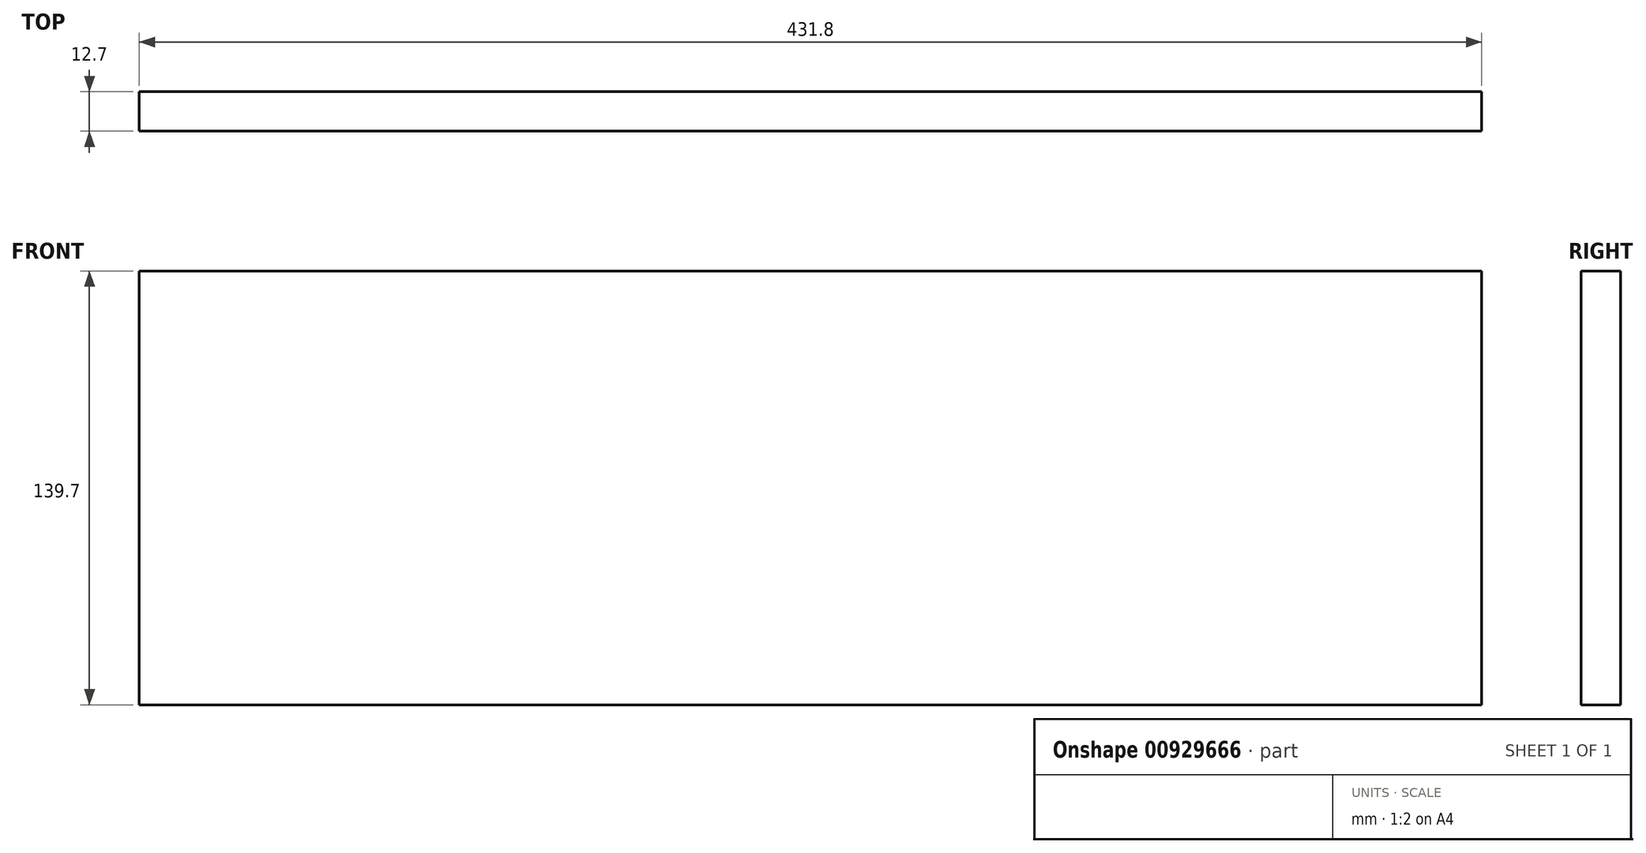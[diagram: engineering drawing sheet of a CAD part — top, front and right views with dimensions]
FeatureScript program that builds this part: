
annotation { "Feature Type Name" : "Feature", "Feature Type Description" : "" }
export const myFeature = defineFeature(function(context is Context, id is Id, definition is map)
    precondition{}
    {
        {
            var Q0;
            Q0=qCreatedBy(makeId("Front.planeOp"),FACE);
            var sketch = newSketch(context, id + "F0", { "sketchPlane" : qUnion([Q0])});
            skLineSegment(sketch, "E0.bottom", {"start": v(67.65, 7.17) * mm, "end": v(-364.15, 7.17) * mm});
            skLineSegment(sketch, "E0.top", {"start": v(67.65, 146.87) * mm, "end": v(-364.15, 146.87) * mm});
            skLineSegment(sketch, "E0.left", {"start": v(67.65, 7.17) * mm, "end": v(67.65, 146.87) * mm});
            skLineSegment(sketch, "E0.right", {"start": v(-364.15, 7.17) * mm, "end": v(-364.15, 146.87) * mm});
            skPoint(sketch, "E0.middle", {"position": v(-148.25, 77.02) * mm});
            skSolve(sketch);
        }
        {
            var Q0;
            Q0=makeQuery(id+"F0.imprint","IMPRINT",FACE,{"disambiguationData":[TD([[makeQuery(id+"F0.imprint","IMPRINT",EDGE,{"derivedFrom":sQuery(id+"F0.wireOp",EDGE,"E0.bottom")}),-1.0]])]});
            extrude(context, id + "F1", {"entities" : qUnion([Q0]), "depth" : 12.7 * mm, "offsetDistance" : 25.4 * mm});
        }
    });
